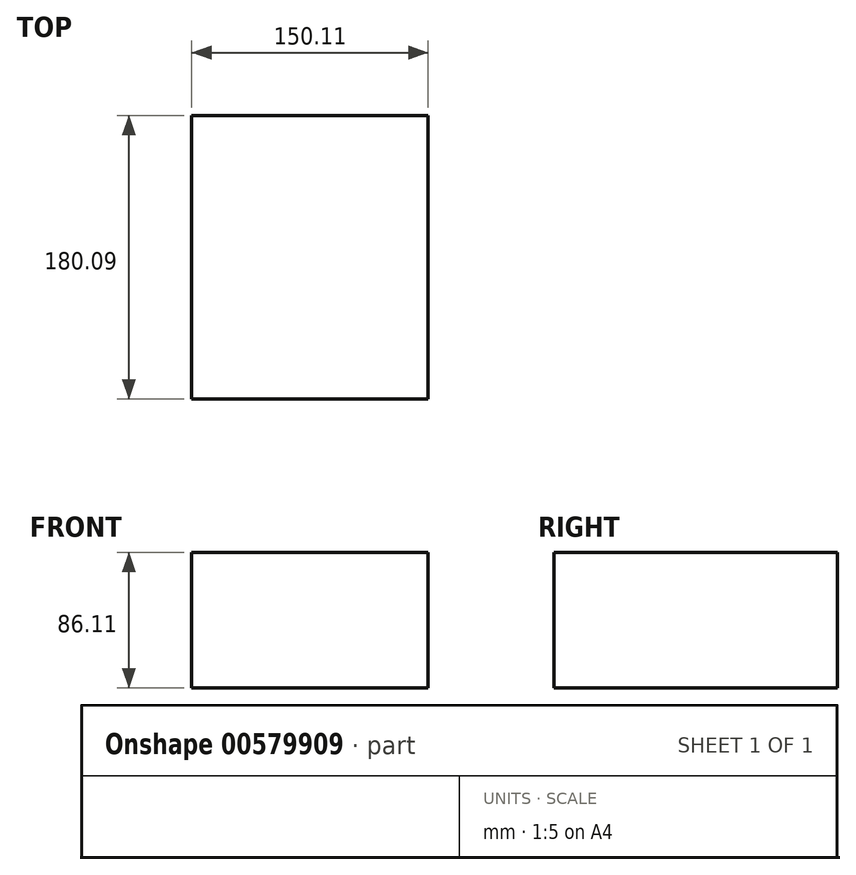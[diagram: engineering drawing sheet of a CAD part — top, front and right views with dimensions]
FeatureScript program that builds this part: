
annotation { "Feature Type Name" : "Feature", "Feature Type Description" : "" }
export const myFeature = defineFeature(function(context is Context, id is Id, definition is map)
    precondition{}
    {
        {
            var Q0;
            Q0=qCreatedBy(makeId("Top.planeOp"),FACE);
            var sketch = newSketch(context, id + "F0", { "sketchPlane" : qUnion([Q0])});
            skLineSegment(sketch, "E0.bottom", {"start": v(0, 0) * mm, "end": v(150.11, 0) * mm});
            skLineSegment(sketch, "E0.top", {"start": v(0, 180.09) * mm, "end": v(150.11, 180.09) * mm});
            skLineSegment(sketch, "E0.left", {"start": v(0, 0) * mm, "end": v(0, 180.09) * mm});
            skLineSegment(sketch, "E0.right", {"start": v(150.11, 0) * mm, "end": v(150.11, 180.09) * mm});
            skSolve(sketch);
        }
        {
            var Q0;
            Q0 = qSketchRegion(id + "F0", true);
            extrude(context, id + "F1", {"entities" : qUnion([Q0]), "depth" : 86.1 * mm, "offsetDistance" : 25.4 * mm});
        }
    });
